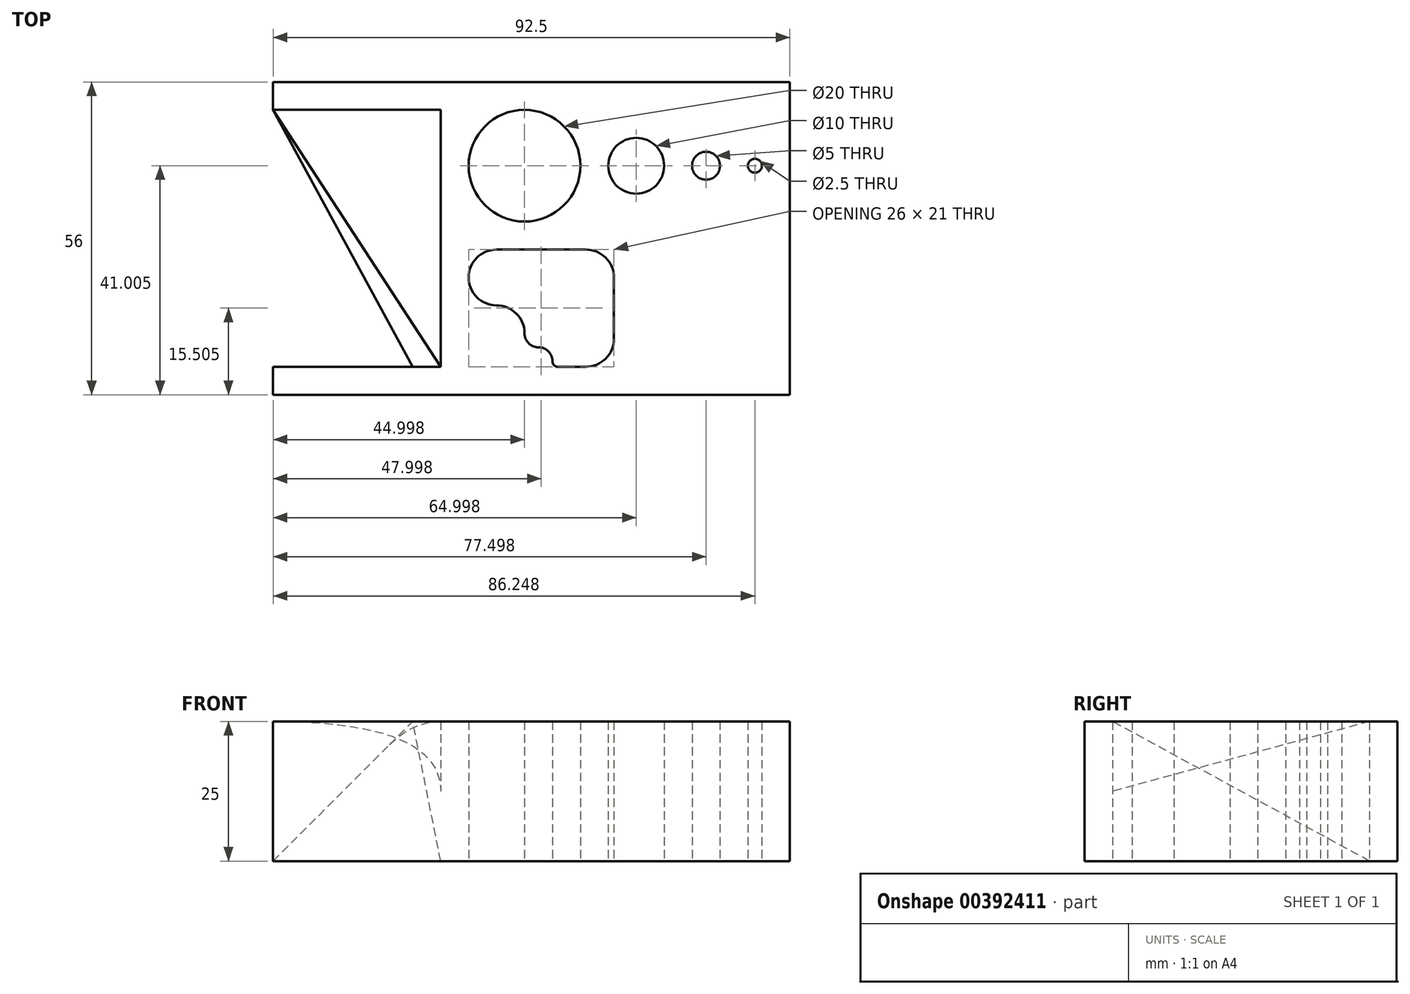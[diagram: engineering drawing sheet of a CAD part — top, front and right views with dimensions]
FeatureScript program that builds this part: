
annotation { "Feature Type Name" : "Feature", "Feature Type Description" : "" }
export const myFeature = defineFeature(function(context is Context, id is Id, definition is map)
    precondition{}
    {
        {
            var Q0;
            Q0=qCreatedBy(makeId("Top.planeOp"),FACE);
            var sketch = newSketch(context, id + "F0", { "sketchPlane" : qUnion([Q0])});
            skLineSegment(sketch, "E0.bottom", {"start": v(32.54, 34.03) * mm, "end": v(-29.96, 34.03) * mm});
            skLineSegment(sketch, "E0.top", {"start": v(32.54, -21.97) * mm, "end": v(-29.96, -21.97) * mm});
            skLineSegment(sketch, "E0.left", {"start": v(32.54, 34.03) * mm, "end": v(32.54, -21.97) * mm});
            skLineSegment(sketch, "E0.right", {"start": v(-29.96, 34.03) * mm, "end": v(-29.96, -21.97) * mm});
            skLineSegment(sketch, "E1.bottom", {"start": v(-29.96, 34.03) * mm, "end": v(-59.96, 34.03) * mm});
            skLineSegment(sketch, "E1.top", {"start": v(-29.96, 29.03) * mm, "end": v(-59.96, 29.03) * mm});
            skLineSegment(sketch, "E1.left", {"start": v(-29.96, 34.03) * mm, "end": v(-29.96, 29.03) * mm});
            skLineSegment(sketch, "E1.right", {"start": v(-59.96, 34.03) * mm, "end": v(-59.96, 29.03) * mm});
            skLineSegment(sketch, "E2.bottom", {"start": v(-29.96, -21.97) * mm, "end": v(-59.96, -21.97) * mm});
            skLineSegment(sketch, "E2.top", {"start": v(-29.96, -16.97) * mm, "end": v(-59.96, -16.97) * mm});
            skLineSegment(sketch, "E2.left", {"start": v(-29.96, -21.97) * mm, "end": v(-29.96, -16.97) * mm});
            skLineSegment(sketch, "E2.right", {"start": v(-59.96, -21.97) * mm, "end": v(-59.96, -16.97) * mm});
            skCircle(sketch, "E3", {"center": v(-14.96, 19.03) * mm, "radius": 10 * mm});
            skCircle(sketch, "E4", {"center": v(5.04, 19.03) * mm, "radius": 5 * mm});
            skCircle(sketch, "E5", {"center": v(17.54, 19.03) * mm, "radius": 2.5 * mm});
            skCircle(sketch, "E6", {"center": v(26.29, 19.03) * mm, "radius": 1.25 * mm});
            skLineSegment(sketch, "E7", {"start": v(-51.58, 19.03) * mm, "end": v(112.9, 19.03) * mm, "construction": true});
            skLineSegment(sketch, "E8", {"start": v(-24.96, -0.97) * mm, "end": v(-24.96, -0.97) * mm});
            skLineSegment(sketch, "E9", {"start": v(-19.96, -5.97) * mm, "end": v(-19.96, -5.97) * mm});
            skLineSegment(sketch, "E10", {"start": v(-14.96, -10.97) * mm, "end": v(-14.96, -10.97) * mm});
            skLineSegment(sketch, "E11", {"start": v(-12.46, -13.47) * mm, "end": v(-12.46, -13.47) * mm});
            skLineSegment(sketch, "E12", {"start": v(-9.96, -15.97) * mm, "end": v(-9.96, -15.97) * mm});
            skLineSegment(sketch, "E13", {"start": v(-8.96, -16.97) * mm, "end": v(-3.96, -16.97) * mm});
            skLineSegment(sketch, "E14", {"start": v(1.04, -11.97) * mm, "end": v(1.04, -0.97) * mm});
            skLineSegment(sketch, "E15", {"start": v(-3.96, 4.03) * mm, "end": v(-19.96, 4.03) * mm});
            skPoint(sketch, "E16.visualSharp", {"position": v(-24.96, -5.97) * mm});
            skArc(sketch, "E16.filletArc", {"start": v(-24.96, -0.97) * mm, "mid": v(-23.5, -4.5) * mm, "end": v(-19.96, -5.97) * mm});
            skPoint(sketch, "E17.visualSharp", {"position": v(-14.96, -5.97) * mm});
            skArc(sketch, "E17.filletArc", {"start": v(-14.96, -10.97) * mm, "mid": v(-16.43, -7.43) * mm, "end": v(-19.96, -5.97) * mm});
            skPoint(sketch, "E18.visualSharp", {"position": v(-14.96, -13.47) * mm});
            skArc(sketch, "E18.filletArc", {"start": v(-14.96, -10.97) * mm, "mid": v(-14.23, -12.73) * mm, "end": v(-12.46, -13.47) * mm});
            skPoint(sketch, "E19.visualSharp", {"position": v(-9.96, -13.47) * mm});
            skArc(sketch, "E19.filletArc", {"start": v(-9.96, -15.97) * mm, "mid": v(-10.7, -14.2) * mm, "end": v(-12.46, -13.47) * mm});
            skPoint(sketch, "E20.visualSharp", {"position": v(-9.96, -16.97) * mm});
            skArc(sketch, "E20.filletArc", {"start": v(-9.96, -15.97) * mm, "mid": v(-9.67, -16.67) * mm, "end": v(-8.96, -16.97) * mm});
            skPoint(sketch, "E21.visualSharp", {"position": v(-24.96, 4.03) * mm});
            skArc(sketch, "E21.filletArc", {"start": v(-19.96, 4.03) * mm, "mid": v(-23.5, 2.57) * mm, "end": v(-24.96, -0.97) * mm});
            skPoint(sketch, "E22.visualSharp", {"position": v(1.04, 4.03) * mm});
            skArc(sketch, "E22.filletArc", {"start": v(1.04, -0.97) * mm, "mid": v(-0.43, 2.57) * mm, "end": v(-3.96, 4.03) * mm});
            skPoint(sketch, "E23.visualSharp", {"position": v(1.04, -16.97) * mm});
            skArc(sketch, "E23.filletArc", {"start": v(-3.96, -16.97) * mm, "mid": v(-0.43, -15.5) * mm, "end": v(1.04, -11.97) * mm});
            skSolve(sketch);
        }
        {
            var Q0;
            Q0=qSketchRegion(id+"F0",true);
            extrude(context, id + "F1", {"entities" : qUnion([Q0]), "depth" : 25 * mm});
        }
        {
            var Q0;
            Q0=makeQuery(id+"F1.opExtrude","SWEPT_FACE",FACE,{"disambiguationData":[OSD([sQuery(id+"F0.wireOp",EDGE,"E1.top")])]});
            var sketch = newSketch(context, id + "F2", { "sketchPlane" : qUnion([Q0])});
            skLineSegment(sketch, "E24.bottom", {"start": v(-29.96, 25) * mm, "end": v(-59.96, 25) * mm});
            skLineSegment(sketch, "E24.top", {"start": v(-29.96, 0) * mm, "end": v(-59.96, 0) * mm});
            skLineSegment(sketch, "E24.left", {"start": v(-29.96, 25) * mm, "end": v(-29.96, 0) * mm});
            skLineSegment(sketch, "E24.right", {"start": v(-59.96, 25) * mm, "end": v(-59.96, 0) * mm});
            skSolve(sketch);
        }
        {
            var Q0;
            Q0=makeQuery(id+"F1.opExtrude","SWEPT_FACE",FACE,{"disambiguationData":[OSD([sQuery(id+"F0.wireOp",EDGE,"E2.top")])]});
            var sketch = newSketch(context, id + "F3", { "sketchPlane" : qUnion([Q0])});
            skLineSegment(sketch, "E25", {"start": v(29.96, 25) * mm, "end": v(29.96, 0) * mm});
            skLineSegment(sketch, "E26", {"start": v(29.96, 0) * mm, "end": v(34.96, 25) * mm});
            skLineSegment(sketch, "E27", {"start": v(34.96, 25) * mm, "end": v(29.96, 25) * mm});
            skSolve(sketch);
        }
        {
            var Q1;
            Q1=qSketchRegion(id+"F2",true);
            var Q2;
            Q2=qSketchRegion(id+"F3",true);
            loft(context, id + "F4", {"operationType" : NewBodyOperationType.ADD, "sheetProfilesArray" : [{ "sheetProfileEntities" : qUnion([Q1]) }, { "sheetProfileEntities" : qUnion([Q2]) }]});
        }
    });
